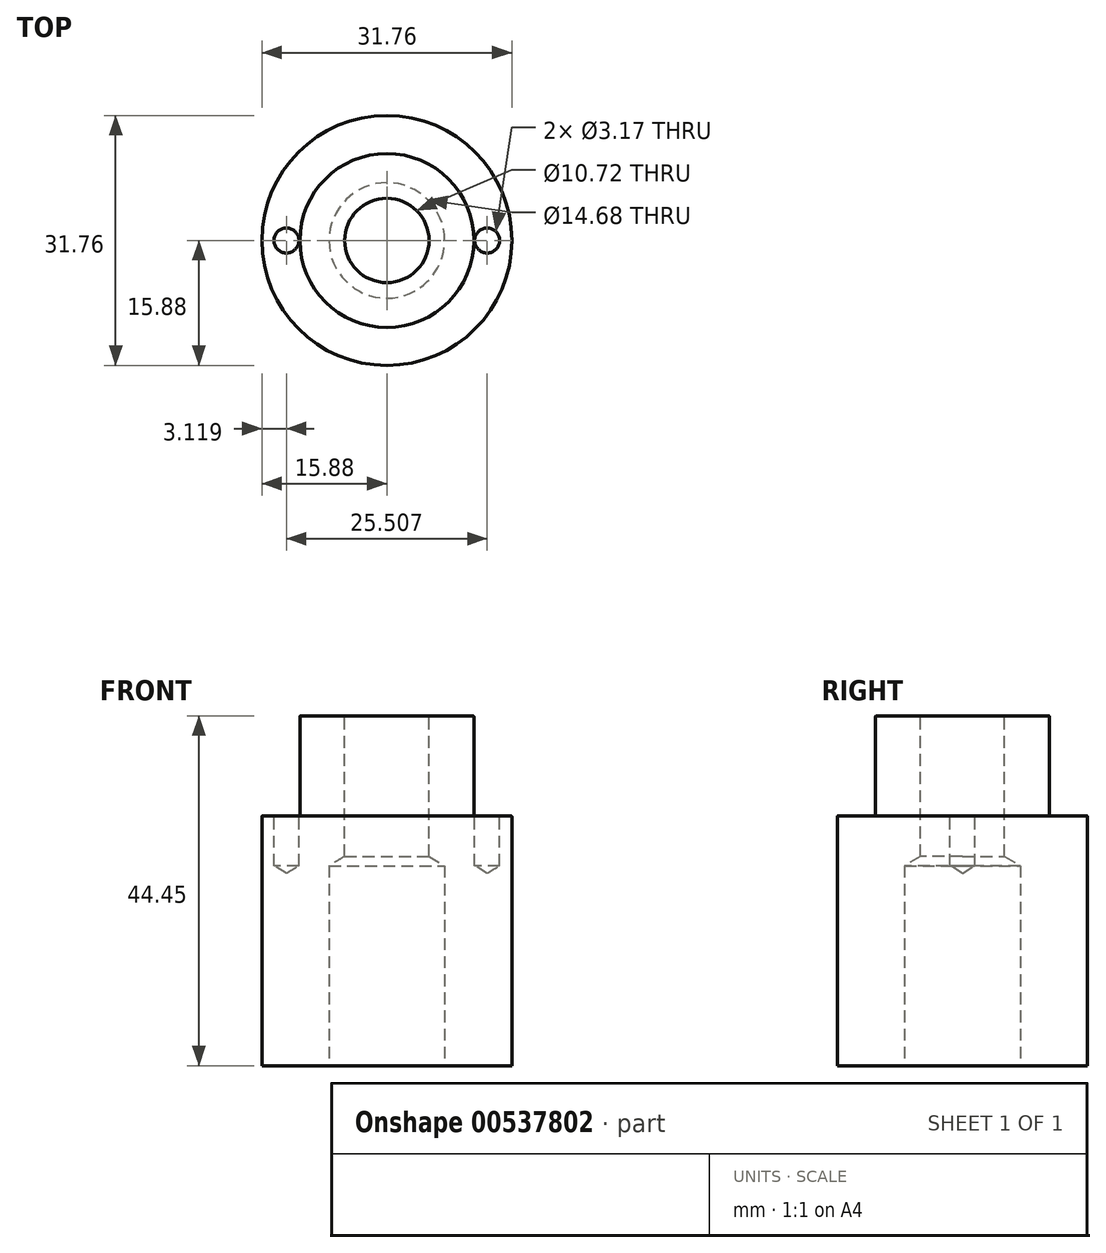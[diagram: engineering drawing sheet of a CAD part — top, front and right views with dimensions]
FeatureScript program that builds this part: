
annotation { "Feature Type Name" : "Feature", "Feature Type Description" : "" }
export const myFeature = defineFeature(function(context is Context, id is Id, definition is map)
    precondition{}
    {
        {
            var Q0;
            Q0=qCreatedBy(makeId("Top.planeOp"),FACE);
            var sketch = newSketch(context, id + "F0", { "sketchPlane" : qUnion([Q0])});
            skCircle(sketch, "E0", {"center": v(0, 0) * mm, "radius": 15.88 * mm});
            skSolve(sketch);
        }
        {
            var Q0;
            Q0 = qSketchRegion(id + "F0", true);
            extrude(context, id + "F1", {"entities" : qUnion([Q0]), "depth" : 31.75 * mm, "offsetDistance" : 25.4 * mm});
        }
        {
            var Q0;
            Q0=makeQuery(id+"F1.opExtrude","CAP_FACE",FACE,{"disambiguationData":[OSD([sQuery(id+"F0.wireOp",EDGE,"E0")])],"isStart":false});
            var sketch = newSketch(context, id + "F2", { "sketchPlane" : qUnion([Q0])});
            skCircle(sketch, "E1", {"center": v(0, 0) * mm, "radius": 11.05 * mm});
            skSolve(sketch);
        }
        {
            var Q0;
            Q0 = qSketchRegion(id + "F2", true);
            extrude(context, id + "F3", {"entities" : qUnion([Q0]), "operationType" : NewBodyOperationType.ADD, "depth" : 12.7 * mm, "offsetDistance" : 25.4 * mm});
        }
        {
            var Q0;
            Q0=makeQuery(id+"F3.opExtrude","CAP_FACE",FACE,{"disambiguationData":[OSD([sQuery(id+"F2.wireOp",EDGE,"E1")])],"isStart":false});
            var sketch = newSketch(context, id + "F4", { "sketchPlane" : qUnion([Q0])});
            skCircle(sketch, "E2", {"center": v(0, 0) * mm, "radius": 5.36 * mm});
            skSolve(sketch);
        }
        {
            var Q0;
            Q0=sQuery(id+"F4.wireOp",VERTEX,"E2.center");
            var Q1;
            Q1=makeQuery(id+"F1.opExtrude","SWEPT_BODY",BODY,{"disambiguationData":[OSD([sQuery(id+"F0.wireOp",EDGE,"E0")])]});
            hole(context, id + "F5", {"style" : HoleStyle.SIMPLE, "endStyle" : HoleEndStyle.BLIND, "standardTappedOrClearance" : lookupTablePath({ "standard" : "ANSI", "engagement" : "75%", "pitch" : "13 tpi", "size" : "1/2", "type" : "Tapped" }), "standardBlindInLast" : lookupTablePath({ "standard" : "ANSI", "engagement" : "75%", "pitch" : "13 tpi", "size" : "1/2", "type" : "Tapped" }), "holeDiameter" : 10.72 * mm, "showTappedDepth" : true, "holeDepth" : 18.56 * mm, "tappedDepth" : 12.7 * mm, "tapClearance" : 3, "startFromSketch" : true, "locations" : qUnion([Q0]), "scope" : qUnion([Q1]), "majorDiameter" : 12.7 * mm});
        }
        {
            var Q0;
            Q0=makeQuery(id+"F1.opExtrude","CAP_FACE",FACE,{"disambiguationData":[OSD([sQuery(id+"F0.wireOp",EDGE,"E0")])],"isStart":false});
            var sketch = newSketch(context, id + "F6", { "sketchPlane" : qUnion([Q0])});
            skCircle(sketch, "E3", {"center": v(12.75, 0) * mm, "radius": 1.59 * mm});
            skCircle(sketch, "E4", {"center": v(-12.76, 0) * mm, "radius": 1.59 * mm});
            skSolve(sketch);
        }
        {
            var Q0;
            Q0=sQuery(id+"F6.wireOp",VERTEX,"E4.center");
            var Q1;
            Q1=sQuery(id+"F6.wireOp",VERTEX,"E3.center");
            var Q2;
            Q2=makeQuery(id+"F1.opExtrude","SWEPT_BODY",BODY,{"disambiguationData":[OSD([sQuery(id+"F0.wireOp",EDGE,"E0")])]});
            hole(context, id + "F7", {"style" : HoleStyle.SIMPLE, "endStyle" : HoleEndStyle.BLIND, "holeDiameter" : 3.17 * mm, "holeDepth" : 6.35 * mm, "tappedDepth" : 12.7 * mm, "tapClearance" : 3, "locations" : qUnion([Q0, Q1]), "scope" : qUnion([Q2])});
        }
        {
            var Q0;
            Q0=makeQuery(id+"F3.opExtrude","CAP_EDGE",EDGE,{"disambiguationData":[OSD([sQuery(id+"F2.wireOp",EDGE,"E1")])],"isStart":false});
            var Q1;
            Q1=makeQuery(id+"F1.opExtrude","CAP_EDGE",EDGE,{"disambiguationData":[OSD([sQuery(id+"F0.wireOp",EDGE,"E0")])],"isStart":false});
            fillet(context, id + "F8", {"entities" : qUnion([Q0, Q1]), "radius" : 0.13 * mm, "tangentPropagation" : true, "allowEdgeOverflow" : false});
        }
        {
            var Q0;
            Q0=makeQuery(id+"F1.opExtrude","CAP_FACE",FACE,{"disambiguationData":[OSD([sQuery(id+"F0.wireOp",EDGE,"E0")])],"isStart":true});
            var sketch = newSketch(context, id + "F9", { "sketchPlane" : qUnion([Q0])});
            skCircle(sketch, "E5", {"center": v(0, 0) * mm, "radius": 0.95 * mm});
            skSolve(sketch);
        }
        {
            var Q0;
            Q0=sQuery(id+"F9.wireOp",VERTEX,"E5.center");
            var Q1;
            Q1=makeQuery(id+"F1.opExtrude","SWEPT_BODY",BODY,{"disambiguationData":[OSD([sQuery(id+"F0.wireOp",EDGE,"E0")])]});
            hole(context, id + "F10", {"style" : HoleStyle.SIMPLE, "endStyle" : HoleEndStyle.BLIND, "standardTappedOrClearance" : lookupTablePath({ "standard" : "ANSI", "engagement" : "75%", "pitch" : "18 tpi", "size" : "5/8", "type" : "Tapped" }), "standardBlindInLast" : lookupTablePath({ "standard" : "ANSI", "engagement" : "75%", "pitch" : "18 tpi", "size" : "5/8", "type" : "Tapped" }), "holeDiameter" : 14.68 * mm, "showTappedDepth" : true, "holeDepth" : 25.4 * mm, "tappedDepth" : 21.17 * mm, "tapClearance" : 3, "startFromSketch" : true, "locations" : qUnion([Q0]), "scope" : qUnion([Q1]), "majorDiameter" : 15.88 * mm});
        }
    });
